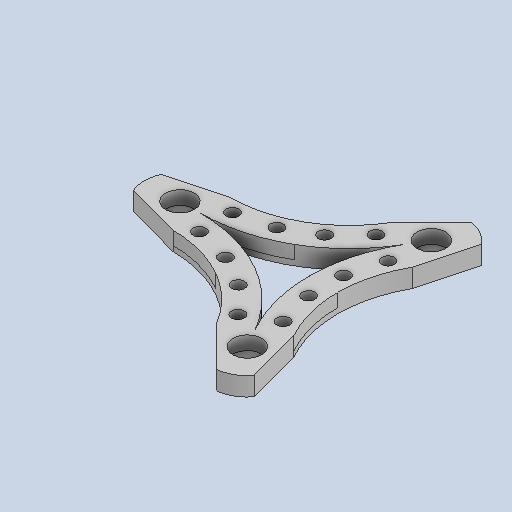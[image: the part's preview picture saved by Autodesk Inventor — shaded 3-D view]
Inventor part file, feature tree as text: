
AUTODESK INVENTOR PART (.ipt)
format: ipt  version: 2022.4 (Build 264492010, 492A)  size: 216,576 bytes
history: native  units: mm
features: other x3, extrude x1, sketch x1
ambient origin geometry x8: Origin, YZ Plane, XZ Plane, XY Plane, X Axis, Y Axis, Z Axis, Center Point
bodies: Solid1 (feature_tree)
feature tree (5):
  other  "Fidget_bottom_3cm.ipt"
  extrude  "Extrusion1"  Depth=10.0mm TaperAngle=360.0deg
  other  "Solid4::Fidget_bottom_3cm.ipt"
  other  "TaggingFeature1"
  sketch  "Sketch1"  dims[d0=10.0mm d1=30.0mm d3=360.0deg d5=10.0mm d6=0.0mm]
